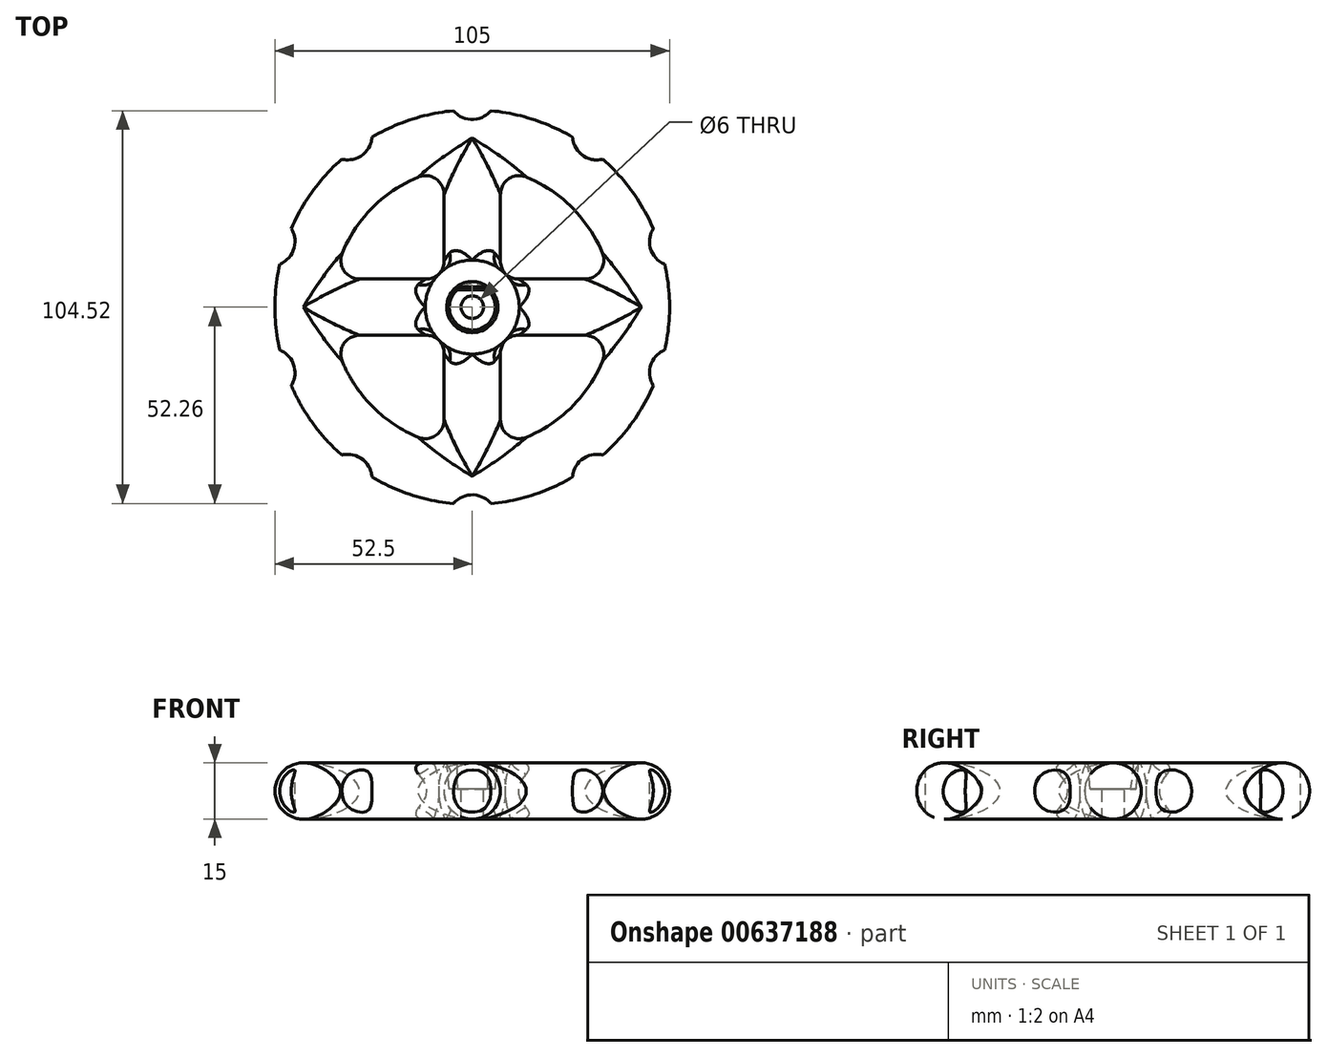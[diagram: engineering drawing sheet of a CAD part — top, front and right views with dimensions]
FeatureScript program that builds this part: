
annotation { "Feature Type Name" : "Feature", "Feature Type Description" : "" }
export const myFeature = defineFeature(function(context is Context, id is Id, definition is map)
    precondition{}
    {
        {
            var Q0;
            Q0=qCreatedBy(makeId("Top.planeOp"),FACE);
            var sketch = newSketch(context, id + "F0", { "sketchPlane" : qUnion([Q0])});
            skCircle(sketch, "E0", {"center": v(0, 0) * mm, "radius": 45 * mm});
            skCircle(sketch, "E1", {"center": v(0, 56.44) * mm, "radius": 6.5 * mm});
            skCircle(sketch, "E2.1.0", {"center": v(-33.17, 45.66) * mm, "radius": 6.5 * mm});
            skCircle(sketch, "E2.2.0", {"center": v(-53.67, 17.44) * mm, "radius": 6.5 * mm});
            skCircle(sketch, "E2.3.0", {"center": v(-53.67, -17.44) * mm, "radius": 6.5 * mm});
            skCircle(sketch, "E2.4.0", {"center": v(-33.17, -45.66) * mm, "radius": 6.5 * mm});
            skCircle(sketch, "E2.5.0", {"center": v(0, -56.44) * mm, "radius": 6.5 * mm});
            skCircle(sketch, "E2.6.0", {"center": v(33.17, -45.66) * mm, "radius": 6.5 * mm});
            skCircle(sketch, "E2.7.0", {"center": v(53.67, -17.44) * mm, "radius": 6.5 * mm});
            skCircle(sketch, "E2.8.0", {"center": v(53.67, 17.44) * mm, "radius": 6.5 * mm});
            skCircle(sketch, "E2.9.0", {"center": v(33.17, 45.66) * mm, "radius": 6.5 * mm});
            skSolve(sketch);
        }
        {
            var Q0;
            Q0=qCreatedBy(makeId("Front.planeOp"),FACE);
            var sketch = newSketch(context, id + "F1", { "sketchPlane" : qUnion([Q0])});
            skCircle(sketch, "E3", {"center": v(-45, 0) * mm, "radius": 7.5 * mm});
            skSolve(sketch);
        }
        {
            var Q0;
            Q0=makeQuery(id+"F1.imprint","IMPRINT",FACE,{"disambiguationData":[TD([[makeQuery(id+"F1.imprint","IMPRINT",EDGE,{"derivedFrom":sQuery(id+"F1.wireOp",EDGE,"E3")}),1.0]])]});
            var Q1;
            Q1=sQuery(id+"F0.wireOp",EDGE,"E0");
            revolve(context, id + "F2", {"entities" : qUnion([Q0]), "axis" : qUnion([Q1]), "revolveType" : RevolveType.FULL});
        }
        {
            var Q0;
            Q0=qCreatedBy(makeId("Top.planeOp"),FACE);
            var sketch = newSketch(context, id + "F3", { "sketchPlane" : qUnion([Q0])});
            skCircle(sketch, "E4", {"center": v(0, 0) * mm, "radius": 12.5 * mm});
            skSolve(sketch);
        }
        {
            var Q0;
            Q0 = qSketchRegion(id + "F3", true);
            extrude(context, id + "F4", {"entities" : qUnion([Q0]), "endBound" : BoundingType.SYMMETRIC, "depth" : 15 * mm, "offsetDistance" : 25 * mm});
        }
        {
            var Q0;
            Q0=qCreatedBy(makeId("Front.planeOp"),FACE);
            var sketch = newSketch(context, id + "F5", { "sketchPlane" : qUnion([Q0])});
            skCircle(sketch, "E5", {"center": v(0, 0) * mm, "radius": 7.5 * mm});
            skSolve(sketch);
        }
        {
            var Q0;
            Q0 = qSketchRegion(id + "F5", true);
            extrude(context, id + "F6", {"entities" : qUnion([Q0]), "endBound" : BoundingType.SYMMETRIC, "depth" : 90 * mm, "offsetDistance" : 25 * mm});
        }
        {
            var Q0;
            Q0=qCreatedBy(makeId("Right.planeOp"),FACE);
            var sketch = newSketch(context, id + "F7", { "sketchPlane" : qUnion([Q0])});
            skCircle(sketch, "E6", {"center": v(0, 0) * mm, "radius": 7.5 * mm});
            skSolve(sketch);
        }
        {
            var Q0;
            Q0 = qSketchRegion(id + "F7", true);
            extrude(context, id + "F8", {"entities" : qUnion([Q0]), "endBound" : BoundingType.SYMMETRIC, "depth" : 90 * mm, "offsetDistance" : 25 * mm});
        }
        {
            var Q0;
            Q0=makeQuery(id+"F0.imprint","IMPRINT",FACE,{"disambiguationData":[TD([[makeQuery(id+"F0.imprint","IMPRINT",EDGE,{"derivedFrom":sQuery(id+"F0.wireOp",EDGE,"E2.1.0")}),1.0]])]});
            var Q1;
            Q1=makeQuery(id+"F0.imprint","IMPRINT",FACE,{"disambiguationData":[TD([[makeQuery(id+"F0.imprint","IMPRINT",EDGE,{"derivedFrom":sQuery(id+"F0.wireOp",EDGE,"E2.3.0")}),1.0]])]});
            var Q2;
            Q2=makeQuery(id+"F0.imprint","IMPRINT",FACE,{"disambiguationData":[TD([[makeQuery(id+"F0.imprint","IMPRINT",EDGE,{"derivedFrom":sQuery(id+"F0.wireOp",EDGE,"E2.2.0")}),1.0]])]});
            var Q3;
            Q3=makeQuery(id+"F0.imprint","IMPRINT",FACE,{"disambiguationData":[TD([[makeQuery(id+"F0.imprint","IMPRINT",EDGE,{"derivedFrom":sQuery(id+"F0.wireOp",EDGE,"E2.4.0")}),1.0]])]});
            var Q4;
            Q4=makeQuery(id+"F0.imprint","IMPRINT",FACE,{"disambiguationData":[TD([[makeQuery(id+"F0.imprint","IMPRINT",EDGE,{"derivedFrom":sQuery(id+"F0.wireOp",EDGE,"E2.5.0")}),1.0]])]});
            var Q5;
            Q5=makeQuery(id+"F0.imprint","IMPRINT",FACE,{"disambiguationData":[TD([[makeQuery(id+"F0.imprint","IMPRINT",EDGE,{"derivedFrom":sQuery(id+"F0.wireOp",EDGE,"E2.6.0")}),1.0]])]});
            var Q6;
            Q6=makeQuery(id+"F0.imprint","IMPRINT",FACE,{"disambiguationData":[TD([[makeQuery(id+"F0.imprint","IMPRINT",EDGE,{"derivedFrom":sQuery(id+"F0.wireOp",EDGE,"E2.7.0")}),1.0]])]});
            var Q7;
            Q7=makeQuery(id+"F0.imprint","IMPRINT",FACE,{"disambiguationData":[TD([[makeQuery(id+"F0.imprint","IMPRINT",EDGE,{"derivedFrom":sQuery(id+"F0.wireOp",EDGE,"E2.8.0")}),1.0]])]});
            var Q8;
            Q8=makeQuery(id+"F0.imprint","IMPRINT",FACE,{"disambiguationData":[TD([[makeQuery(id+"F0.imprint","IMPRINT",EDGE,{"derivedFrom":sQuery(id+"F0.wireOp",EDGE,"E2.9.0")}),1.0]])]});
            var Q9;
            Q9=makeQuery(id+"F0.imprint","IMPRINT",FACE,{"disambiguationData":[TD([[makeQuery(id+"F0.imprint","IMPRINT",EDGE,{"derivedFrom":sQuery(id+"F0.wireOp",EDGE,"E1")}),1.0]])]});
            extrude(context, id + "F9", {"entities" : qUnion([Q0, Q1, Q2, Q3, Q4, Q5, Q6, Q7, Q8, Q9]), "operationType" : NewBodyOperationType.REMOVE, "endBound" : BoundingType.SYMMETRIC, "oppositeDirection" : true, "depth" : 25 * mm, "offsetDistance" : 25 * mm});
        }
        {
            var Q0;
            Q0=makeQuery(id+"F2.opRevolve","SWEPT_BODY",BODY,{"disambiguationData":[OSD([sQuery(id+"F1.wireOp",EDGE,"E3")])]});
            var Q1;
            Q1=makeQuery(id+"F6.opExtrude","SWEPT_BODY",BODY,{"disambiguationData":[OSD([sQuery(id+"F5.wireOp",EDGE,"E5")])]});
            var Q2;
            Q2=makeQuery(id+"F8.opExtrude","SWEPT_BODY",BODY,{"disambiguationData":[OSD([sQuery(id+"F7.wireOp",EDGE,"E6")])]});
            booleanBodies(context, id + "F10", {"operationType" : BooleanOperationType.UNION, "tools" : qUnion([Q0, Q1, Q2])});
        }
        {
            var Q0;
            Q0=makeQuery(id+"F10.opBoolean","INTERSECT",EDGE,{"disambiguationData":[OD(2.0)],"derivedFrom":[makeQuery(id+"F6.opExtrude","SWEPT_FACE",FACE,{"disambiguationData":[OSD([sQuery(id+"F5.wireOp",EDGE,"E5")])]}),makeQuery(id+"F2.opRevolve","SWEPT_FACE",FACE,{"disambiguationData":[OSD([sQuery(id+"F1.wireOp",EDGE,"E3")])]})]});
            var Q1;
            Q1=makeQuery(id+"F10.opBoolean","INTERSECT",EDGE,{"disambiguationData":[OD(3.0)],"derivedFrom":[makeQuery(id+"F6.opExtrude","SWEPT_FACE",FACE,{"disambiguationData":[OSD([sQuery(id+"F5.wireOp",EDGE,"E5")])]}),makeQuery(id+"F2.opRevolve","SWEPT_FACE",FACE,{"disambiguationData":[OSD([sQuery(id+"F1.wireOp",EDGE,"E3")])]})]});
            var Q2;
            Q2=makeQuery(id+"F10.opBoolean","INTERSECT",EDGE,{"disambiguationData":[OD(3.0)],"derivedFrom":[makeQuery(id+"F8.opExtrude","SWEPT_FACE",FACE,{"disambiguationData":[OSD([sQuery(id+"F7.wireOp",EDGE,"E6")])]}),makeQuery(id+"F2.opRevolve","SWEPT_FACE",FACE,{"disambiguationData":[OSD([sQuery(id+"F1.wireOp",EDGE,"E3")])]})]});
            var Q3;
            Q3=makeQuery(id+"F10.opBoolean","INTERSECT",EDGE,{"disambiguationData":[OD(2.0)],"derivedFrom":[makeQuery(id+"F8.opExtrude","SWEPT_FACE",FACE,{"disambiguationData":[OSD([sQuery(id+"F7.wireOp",EDGE,"E6")])]}),makeQuery(id+"F2.opRevolve","SWEPT_FACE",FACE,{"disambiguationData":[OSD([sQuery(id+"F1.wireOp",EDGE,"E3")])]})]});
            var Q4;
            Q4=makeQuery(id+"F10.opBoolean","INTERSECT",EDGE,{"disambiguationData":[OD(1.0)],"derivedFrom":[makeQuery(id+"F6.opExtrude","SWEPT_FACE",FACE,{"disambiguationData":[OSD([sQuery(id+"F5.wireOp",EDGE,"E5")])]}),makeQuery(id+"F2.opRevolve","SWEPT_FACE",FACE,{"disambiguationData":[OSD([sQuery(id+"F1.wireOp",EDGE,"E3")])]})]});
            var Q5;
            Q5=makeQuery(id+"F10.opBoolean","INTERSECT",EDGE,{"disambiguationData":[OD(0.0)],"derivedFrom":[makeQuery(id+"F6.opExtrude","SWEPT_FACE",FACE,{"disambiguationData":[OSD([sQuery(id+"F5.wireOp",EDGE,"E5")])]}),makeQuery(id+"F2.opRevolve","SWEPT_FACE",FACE,{"disambiguationData":[OSD([sQuery(id+"F1.wireOp",EDGE,"E3")])]})]});
            var Q6;
            Q6=makeQuery(id+"F10.opBoolean","INTERSECT",EDGE,{"disambiguationData":[OD(0.0)],"derivedFrom":[makeQuery(id+"F8.opExtrude","SWEPT_FACE",FACE,{"disambiguationData":[OSD([sQuery(id+"F7.wireOp",EDGE,"E6")])]}),makeQuery(id+"F2.opRevolve","SWEPT_FACE",FACE,{"disambiguationData":[OSD([sQuery(id+"F1.wireOp",EDGE,"E3")])]})]});
            var Q7;
            Q7=makeQuery(id+"F10.opBoolean","INTERSECT",EDGE,{"disambiguationData":[OD(1.0)],"derivedFrom":[makeQuery(id+"F8.opExtrude","SWEPT_FACE",FACE,{"disambiguationData":[OSD([sQuery(id+"F7.wireOp",EDGE,"E6")])]}),makeQuery(id+"F2.opRevolve","SWEPT_FACE",FACE,{"disambiguationData":[OSD([sQuery(id+"F1.wireOp",EDGE,"E3")])]})]});
            fillet(context, id + "F11", {"entities" : qUnion([Q0, Q1, Q2, Q3, Q4, Q5, Q6, Q7]), "radius" : 5 * mm, "tangentPropagation" : true, "allowEdgeOverflow" : false});
        }
        {
            var Q0;
            Q0=makeQuery(id+"F2.opRevolve","SWEPT_BODY",BODY,{"disambiguationData":[OSD([sQuery(id+"F1.wireOp",EDGE,"E3")])]});
            var Q1;
            Q1=makeQuery(id+"F4.opExtrude","SWEPT_BODY",BODY,{"disambiguationData":[OSD([sQuery(id+"F3.wireOp",EDGE,"E4")])]});
            booleanBodies(context, id + "F12", {"operationType" : BooleanOperationType.UNION, "tools" : qUnion([Q0, Q1])});
        }
        {
            var Q0;
            Q0=makeQuery(id+"F12.opBoolean","INTERSECT",EDGE,{"disambiguationData":[OD(1.0)],"derivedFrom":[makeQuery(id+"F4.opExtrude","SWEPT_FACE",FACE,{"disambiguationData":[OSD([sQuery(id+"F3.wireOp",EDGE,"E4")])]}),makeQuery(id+"F10.opBoolean","SPLIT",FACE,{"disambiguationData":[OD(0.0)],"derivedFrom":makeQuery(id+"F8.opExtrude","SWEPT_FACE",FACE,{"disambiguationData":[OSD([sQuery(id+"F7.wireOp",EDGE,"E6")])]})})]});
            var Q1;
            Q1=makeQuery(id+"F12.opBoolean","INTERSECT",EDGE,{"disambiguationData":[OD(0.0)],"derivedFrom":[makeQuery(id+"F4.opExtrude","SWEPT_FACE",FACE,{"disambiguationData":[OSD([sQuery(id+"F3.wireOp",EDGE,"E4")])]}),makeQuery(id+"F10.opBoolean","SPLIT",FACE,{"disambiguationData":[OD(1.0)],"derivedFrom":makeQuery(id+"F6.opExtrude","SWEPT_FACE",FACE,{"disambiguationData":[OSD([sQuery(id+"F5.wireOp",EDGE,"E5")])]})})]});
            var Q2;
            Q2=makeQuery(id+"F12.opBoolean","INTERSECT",EDGE,{"disambiguationData":[OD(1.0)],"derivedFrom":[makeQuery(id+"F4.opExtrude","SWEPT_FACE",FACE,{"disambiguationData":[OSD([sQuery(id+"F3.wireOp",EDGE,"E4")])]}),makeQuery(id+"F10.opBoolean","SPLIT",FACE,{"disambiguationData":[OD(1.0)],"derivedFrom":makeQuery(id+"F6.opExtrude","SWEPT_FACE",FACE,{"disambiguationData":[OSD([sQuery(id+"F5.wireOp",EDGE,"E5")])]})})]});
            var Q3;
            Q3=makeQuery(id+"F12.opBoolean","INTERSECT",EDGE,{"disambiguationData":[OD(1.0)],"derivedFrom":[makeQuery(id+"F4.opExtrude","SWEPT_FACE",FACE,{"disambiguationData":[OSD([sQuery(id+"F3.wireOp",EDGE,"E4")])]}),makeQuery(id+"F10.opBoolean","SPLIT",FACE,{"disambiguationData":[OD(1.0)],"derivedFrom":makeQuery(id+"F8.opExtrude","SWEPT_FACE",FACE,{"disambiguationData":[OSD([sQuery(id+"F7.wireOp",EDGE,"E6")])]})})]});
            var Q4;
            Q4=makeQuery(id+"F12.opBoolean","INTERSECT",EDGE,{"disambiguationData":[OD(0.0)],"derivedFrom":[makeQuery(id+"F4.opExtrude","SWEPT_FACE",FACE,{"disambiguationData":[OSD([sQuery(id+"F3.wireOp",EDGE,"E4")])]}),makeQuery(id+"F10.opBoolean","SPLIT",FACE,{"disambiguationData":[OD(1.0)],"derivedFrom":makeQuery(id+"F8.opExtrude","SWEPT_FACE",FACE,{"disambiguationData":[OSD([sQuery(id+"F7.wireOp",EDGE,"E6")])]})})]});
            var Q5;
            Q5=makeQuery(id+"F12.opBoolean","INTERSECT",EDGE,{"disambiguationData":[OD(1.0)],"derivedFrom":[makeQuery(id+"F4.opExtrude","SWEPT_FACE",FACE,{"disambiguationData":[OSD([sQuery(id+"F3.wireOp",EDGE,"E4")])]}),makeQuery(id+"F10.opBoolean","SPLIT",FACE,{"disambiguationData":[OD(0.0)],"derivedFrom":makeQuery(id+"F6.opExtrude","SWEPT_FACE",FACE,{"disambiguationData":[OSD([sQuery(id+"F5.wireOp",EDGE,"E5")])]})})]});
            var Q6;
            Q6=makeQuery(id+"F12.opBoolean","INTERSECT",EDGE,{"disambiguationData":[OD(0.0)],"derivedFrom":[makeQuery(id+"F4.opExtrude","SWEPT_FACE",FACE,{"disambiguationData":[OSD([sQuery(id+"F3.wireOp",EDGE,"E4")])]}),makeQuery(id+"F10.opBoolean","SPLIT",FACE,{"disambiguationData":[OD(0.0)],"derivedFrom":makeQuery(id+"F6.opExtrude","SWEPT_FACE",FACE,{"disambiguationData":[OSD([sQuery(id+"F5.wireOp",EDGE,"E5")])]})})]});
            var Q7;
            Q7=makeQuery(id+"F12.opBoolean","INTERSECT",EDGE,{"disambiguationData":[OD(0.0)],"derivedFrom":[makeQuery(id+"F4.opExtrude","SWEPT_FACE",FACE,{"disambiguationData":[OSD([sQuery(id+"F3.wireOp",EDGE,"E4")])]}),makeQuery(id+"F10.opBoolean","SPLIT",FACE,{"disambiguationData":[OD(0.0)],"derivedFrom":makeQuery(id+"F8.opExtrude","SWEPT_FACE",FACE,{"disambiguationData":[OSD([sQuery(id+"F7.wireOp",EDGE,"E6")])]})})]});
            fillet(context, id + "F13", {"entities" : qUnion([Q0, Q1, Q2, Q3, Q4, Q5, Q6, Q7]), "radius" : 5 * mm, "tangentPropagation" : true, "allowEdgeOverflow" : false});
        }
        {
            var Q0;
            Q0=qCreatedBy(makeId("Front.planeOp"),FACE);
            var sketch = newSketch(context, id + "F14", { "sketchPlane" : qUnion([Q0])});
            skLineSegment(sketch, "E7", {"start": v(0, 7.5) * mm, "end": v(6.8, 7.5) * mm});
            skLineSegment(sketch, "E8", {"start": v(6.8, 7.5) * mm, "end": v(6.1, 0.5) * mm});
            skLineSegment(sketch, "E9", {"start": v(6.1, 0.5) * mm, "end": v(0, 0.5) * mm});
            skLineSegment(sketch, "E10", {"start": v(0, 0.5) * mm, "end": v(0, 7.5) * mm});
            skSolve(sketch);
        }
        {
            var Q0;
            Q0 = qSketchRegion(id + "F14", true);
            var Q1;
            Q1=sQuery(id+"F14.wireOp",EDGE,"E10");
            revolve(context, id + "F15", {"operationType" : NewBodyOperationType.REMOVE, "entities" : qUnion([Q0]), "axis" : qUnion([Q1]), "revolveType" : RevolveType.FULL, "oppositeDirection" : true});
        }
        {
            var Q0;
            Q0=makeQuery(id+"F15.boolean.opBoolean","COPY",FACE,{"derivedFrom":makeQuery(id+"F15.opRevolve","SWEPT_FACE",FACE,{"disambiguationData":[OSD([sQuery(id+"F14.wireOp",EDGE,"E9")])]})});
            var sketch = newSketch(context, id + "F16", { "sketchPlane" : qUnion([Q0])});
            skCircle(sketch, "E11", {"center": v(0, 0) * mm, "radius": 3 * mm});
            skSolve(sketch);
        }
        {
            var Q0;
            Q0 = qSketchRegion(id + "F16", true);
            extrude(context, id + "F17", {"entities" : qUnion([Q0]), "operationType" : NewBodyOperationType.REMOVE, "endBound" : BoundingType.THROUGH_ALL, "oppositeDirection" : true, "depth" : 25 * mm, "offsetDistance" : 25 * mm});
        }
        {
            var Q0;
            Q0=makeQuery(id+"F15.boolean.opBoolean","COPY",FACE,{"derivedFrom":makeQuery(id+"F15.opRevolve","SWEPT_FACE",FACE,{"disambiguationData":[OSD([sQuery(id+"F14.wireOp",EDGE,"E9")])]})});
            var sketch = newSketch(context, id + "F18", { "sketchPlane" : qUnion([Q0])});
            skArc(sketch, "E12.0", {"start": v(4, 4.6) * mm, "mid": v(0, 6.1) * mm, "end": v(-4, 4.6) * mm});
            skLineSegment(sketch, "E13", {"start": v(-4, 4.6) * mm, "end": v(4, 4.6) * mm});
            skSolve(sketch);
        }
        {
            var Q0;
            Q0=makeQuery(id+"F4.opExtrude","CAP_FACE",FACE,{"disambiguationData":[OSD([sQuery(id+"F3.wireOp",EDGE,"E4")])],"isStart":false});
            var sketch = newSketch(context, id + "F19", { "sketchPlane" : qUnion([Q0])});
            skArc(sketch, "E14.0", {"start": v(4.13, 5.4) * mm, "mid": v(0, 6.8) * mm, "end": v(-4.13, 5.4) * mm});
            skLineSegment(sketch, "E15", {"start": v(-4.13, 5.4) * mm, "end": v(4.13, 5.4) * mm});
            skSolve(sketch);
        }
        {
            var Q0;
            Q0=makeQuery(id+"F19.imprint","IMPRINT",FACE,{"disambiguationData":[TD([[makeQuery(id+"F19.imprint","IMPRINT",EDGE,{"derivedFrom":sQuery(id+"F19.wireOp",EDGE,"E14.0")}),1.0]])]});
            var Q1;
            Q1=makeQuery(id+"F18.imprint","IMPRINT",FACE,{"disambiguationData":[TD([[makeQuery(id+"F18.imprint","IMPRINT",EDGE,{"derivedFrom":sQuery(id+"F18.wireOp",EDGE,"E12.0")}),1.0]])]});
            loft(context, id + "F20", {"sheetProfilesArray" : [{ "sheetProfileEntities" : qUnion([Q0]) }, { "sheetProfileEntities" : qUnion([Q1]) }]});
        }
    });
